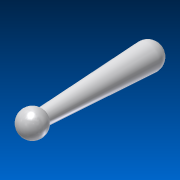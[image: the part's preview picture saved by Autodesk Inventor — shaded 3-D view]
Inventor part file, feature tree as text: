
AUTODESK INVENTOR PART (.ipt)
format: ipt  version: 2011 SP1 (Build 150282100, 282)  size: 108,032 bytes
history: native  units: mm
features: revolve x2, sketch x2, projected_geometry x1
ambient origin geometry x8: Origin, YZ Plane, XZ Plane, XY Plane, X Axis, Y Axis, Z Axis, Center Point
bodies: Solid1 (feature_tree)
feature tree (5):
  revolve  "Revolution1"  [1 undecoded]
  revolve  "Revolution2"  [1 undecoded]
  sketch  "Sketch1"  dims[d1=1.5mm d3=0.875mm]
  sketch  "Sketch2"  dims[d4=180.0deg d5=3.0mm d6=12.5mm d7=180.0deg]
  projected_geometry  "Projected Loop1"
note: 2 required parameter values undecoded (feature->parameter linkage not recoverable at this tier; creation-order binding heuristic only, values carry confidence <= 0.55)
